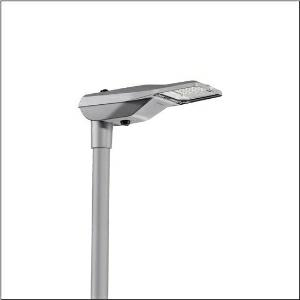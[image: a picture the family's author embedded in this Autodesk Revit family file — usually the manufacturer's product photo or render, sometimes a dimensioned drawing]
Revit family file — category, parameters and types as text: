
# Revit family: streetlight_sl_21_micro___pl52_5xe1h33t08db_704d
name_source: partatom
category: Lighting Fixtures
units: mm (PartAtom-declared; Revit-internal decimal feet)

## family parameters
Cut with Voids When Loaded = No
Host = Face
Light Source = No
Part Type = Normal
Room Calculation Point = No
Round Connector Dimension = Use Diameter
Shared = No

## types (1)
- --- (1 x LED, 5020 lm, 39.1 W, 3000K)
    Apparent Load = 39 VA
    CIE Flux Codes = 27 59 98 100 100
    Color Rendering = 70
    Color Temperature = 3000K
    Default Elevation = 1800 mm
    Description = Streetlight SL 21 micro, mast luminaire, primary light control with lens, of PMMA, primary optical cover: cover, of toughened safety glass, transparent, light distribution: PL52, light emission: direct distribution, primary light characteristic: asymmetric, installation type: side-entry, post-top, LED, High Power LED, rated luminous flux: 5.020lm, luminous efficacy: 128lm/W, light colour: 730, colour temperature: 3000K, control gear: D4i, control: flexible luminous flux parameterisation, time-dependent luminous flux control, constant luminous flux control, overheat protection, pre-setting: logarithmic dimming characteristic, mains connection: 220..240V, AC, 50/60Hz, start of lifetime: 39W, end of service life: 41W, reduction: 18W, luminaire housing, of diecast aluminium, powder-coated, SITECO metallic grey (DB 702S), corrosivity category C5 high according to DIN EN ISO 12944, please order mast flange separately, inclination adjustable: 0°, 5°, 10°, 15°, sealing non-destructively replaceable, multi-level sealing system, length: 528mm, width: 235mm, height: 110mm, mast flange for spigot size: 42mm (side-entry): 5XC10008XM4, 60/48mm (side-entry/post-top): 5XC10108XM2, 76/60mm (side-entry/post-top): 5XC10108XM1, Smart Interface below and above, protection rating (complete): IP66, insulation class (complete): insulation class II (safety insulation), certification: CE, ENEC, ENEC+, VDE, impact resistance: IK10, permissible operating ambient temperature for outdoor applications: -40..+50°C, standard-compliant lighting for roads and squares, packaging unit: 1 piece

Light Distribution: PL52
    Height = 110 mm
    Lamp = 1 x LED
    Lamp Light Flux = 5020 lm
    Lamp Power = 39.1 W
    Lamp count = 1
    Length = 528 mm
    Luminous efficacy = 128 lm/W
    Manufacturer = Siteco
    ModVariant = No
    Model = 5XE1H33T08DB
    Number of Poles = 1
    OnlyDefault = Yes
    Power Factor = 1
    Product Name = Streetlight SL 21 micro | PL52
    Product group = mast luminaire | pylon top
    ProductGroupID = 6100
    Protection Class = Protection class II
    Protection Degree = IP 66
    RLX_Detail_Level = 1
    RLX_Emergency_Light_Flux = 0 lm
    RLX_Emergency_Type = 0
    RLX_Emergency_Type_DB = No
    RlxData = <blob elided: 107865 chars, md5=b2e26a10>
    Socket = socket
    Standby Power = 0 W
    System Light Flux = 5020 lm
    System Power = 39 W
    Type Comments = factory setting: luminous flux: 100 % | dim-lin: 254 | 765 mA
    Type Image = l_1007239.jpg
    URL = http://relux.com
    VarID = @adj_155665
    Voltage = 0 V
    Weight = 0.00 kg
    Width = 235 mm

## geometry (parser evidence)
native form markers: Blend x4, Sweep x10
no freeform markers — native parametric forms only
